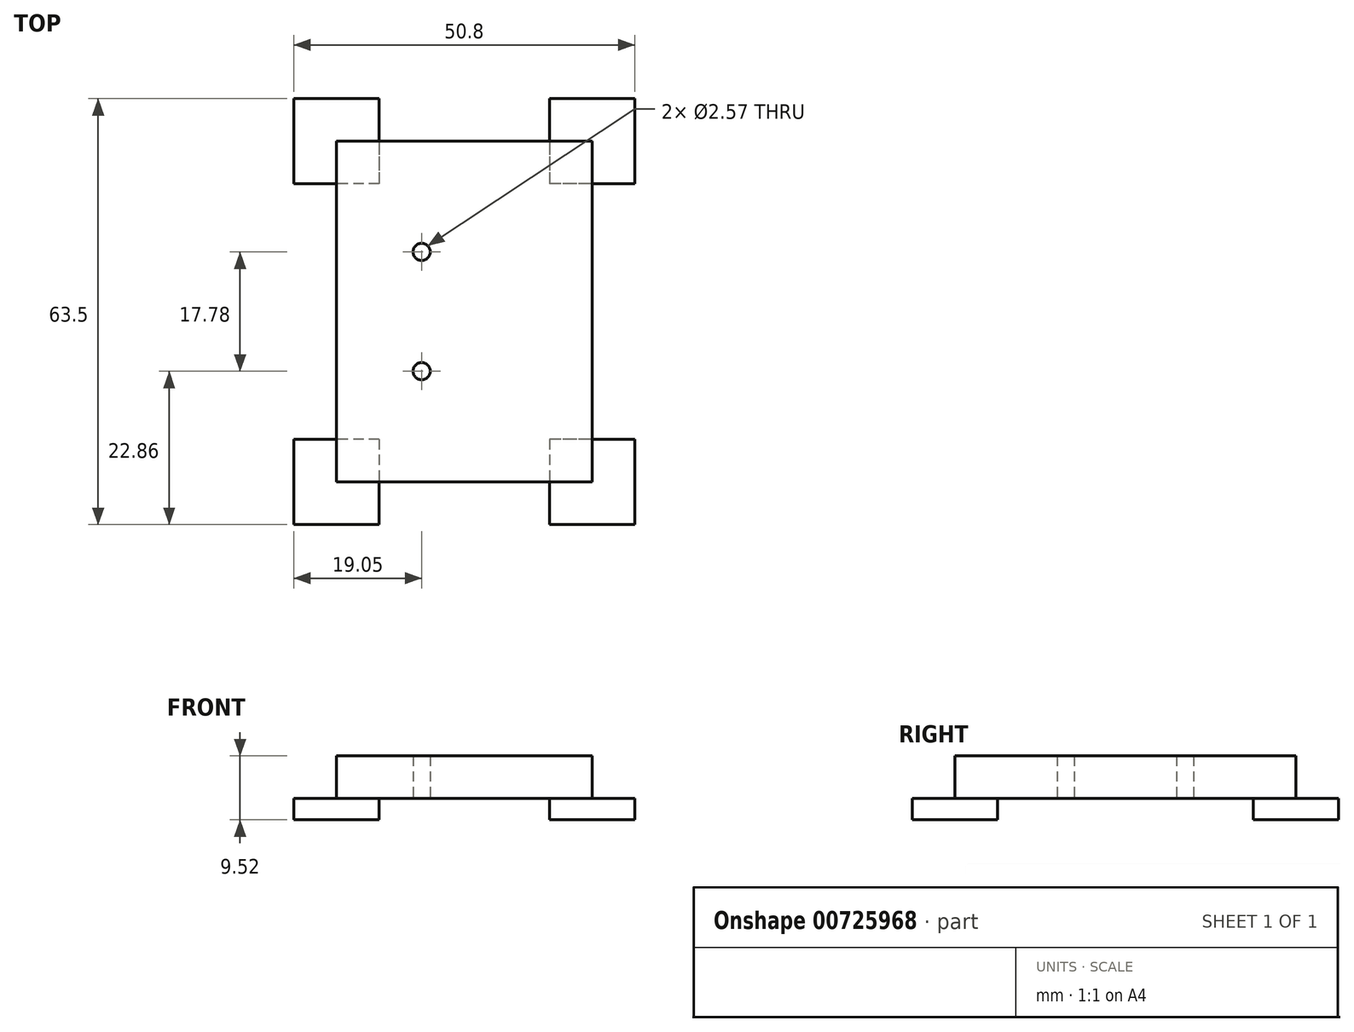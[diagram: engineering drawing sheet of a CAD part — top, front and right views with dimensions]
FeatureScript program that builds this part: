
annotation { "Feature Type Name" : "Feature", "Feature Type Description" : "" }
export const myFeature = defineFeature(function(context is Context, id is Id, definition is map)
    precondition{}
    {
        {
            var Q0;
            Q0=qCreatedBy(makeId("Top.planeOp"),FACE);
            var sketch = newSketch(context, id + "F0", { "sketchPlane" : qUnion([Q0])});
            skLineSegment(sketch, "E0.bottom", {"start": v(0, 0) * mm, "end": v(38.1, 0) * mm});
            skLineSegment(sketch, "E0.top", {"start": v(0, 50.8) * mm, "end": v(38.1, 50.8) * mm});
            skLineSegment(sketch, "E0.left", {"start": v(0, 0) * mm, "end": v(0, 50.8) * mm});
            skLineSegment(sketch, "E0.right", {"start": v(38.1, 0) * mm, "end": v(38.1, 50.8) * mm});
            skSolve(sketch);
        }
        {
            var Q0;
            Q0 = qSketchRegion(id + "F0", true);
            extrude(context, id + "F1", {"entities" : qUnion([Q0]), "depth" : 6.35 * mm, "offsetDistance" : 25.4 * mm});
        }
        {
            var Q0;
            Q0=makeQuery(id+"F1.opExtrude","CAP_FACE",FACE,{"disambiguationData":[OSD([sQuery(id+"F0.wireOp",EDGE,"E0.bottom"),sQuery(id+"F0.wireOp",EDGE,"E0.top"),sQuery(id+"F0.wireOp",EDGE,"E0.left"),sQuery(id+"F0.wireOp",EDGE,"E0.right")])],"isStart":true});
            var sketch = newSketch(context, id + "F2", { "sketchPlane" : qUnion([Q0])});
            skLineSegment(sketch, "E1.bottom", {"start": v(6.35, -6.35) * mm, "end": v(-6.35, -6.35) * mm});
            skLineSegment(sketch, "E1.top", {"start": v(6.35, 6.35) * mm, "end": v(-6.35, 6.35) * mm});
            skLineSegment(sketch, "E1.left", {"start": v(-6.35, -6.35) * mm, "end": v(-6.35, 6.35) * mm});
            skLineSegment(sketch, "E1.right", {"start": v(6.35, -6.35) * mm, "end": v(6.35, 6.35) * mm});
            skLineSegment(sketch, "E2.bottom", {"start": v(44.45, -6.35) * mm, "end": v(31.75, -6.35) * mm});
            skLineSegment(sketch, "E2.top", {"start": v(44.45, 6.35) * mm, "end": v(31.75, 6.35) * mm});
            skLineSegment(sketch, "E2.left", {"start": v(31.75, -6.35) * mm, "end": v(31.75, 6.35) * mm});
            skLineSegment(sketch, "E2.right", {"start": v(44.45, -6.35) * mm, "end": v(44.45, 6.35) * mm});
            skLineSegment(sketch, "E3.bottom", {"start": v(6.35, -57.15) * mm, "end": v(-6.35, -57.15) * mm});
            skLineSegment(sketch, "E3.top", {"start": v(6.35, -44.45) * mm, "end": v(-6.35, -44.45) * mm});
            skLineSegment(sketch, "E3.left", {"start": v(-6.35, -57.15) * mm, "end": v(-6.35, -44.45) * mm});
            skLineSegment(sketch, "E3.right", {"start": v(6.35, -57.15) * mm, "end": v(6.35, -44.45) * mm});
            skLineSegment(sketch, "E4.bottom", {"start": v(44.45, -57.15) * mm, "end": v(31.75, -57.15) * mm});
            skLineSegment(sketch, "E4.top", {"start": v(44.45, -44.45) * mm, "end": v(31.75, -44.45) * mm});
            skLineSegment(sketch, "E4.left", {"start": v(31.75, -57.15) * mm, "end": v(31.75, -44.45) * mm});
            skLineSegment(sketch, "E4.right", {"start": v(44.45, -57.15) * mm, "end": v(44.45, -44.45) * mm});
            skSolve(sketch);
        }
        {
            var Q0;
            Q0 = qSketchRegion(id + "F2", true);
            extrude(context, id + "F3", {"entities" : qUnion([Q0]), "operationType" : NewBodyOperationType.ADD, "depth" : 3.17 * mm, "offsetDistance" : 25.4 * mm});
        }
        {
            var Q0;
            Q0=makeQuery(id+"F1.opExtrude","CAP_FACE",FACE,{"disambiguationData":[OSD([sQuery(id+"F0.wireOp",EDGE,"E0.bottom"),sQuery(id+"F0.wireOp",EDGE,"E0.top"),sQuery(id+"F0.wireOp",EDGE,"E0.left"),sQuery(id+"F0.wireOp",EDGE,"E0.right")])],"isStart":true});
            var sketch = newSketch(context, id + "F4", { "sketchPlane" : qUnion([Q0])});
            skCircle(sketch, "E5", {"center": v(12.7, -16.51) * mm, "radius": 1.28 * mm});
            skCircle(sketch, "E6", {"center": v(12.7, -34.3) * mm, "radius": 1.28 * mm});
            skSolve(sketch);
        }
        {
            var Q0;
            Q0 = qSketchRegion(id + "F4", true);
            extrude(context, id + "F5", {"entities" : qUnion([Q0]), "operationType" : NewBodyOperationType.REMOVE, "oppositeDirection" : true, "depth" : 25.4 * mm, "offsetDistance" : 25.4 * mm});
        }
    });
